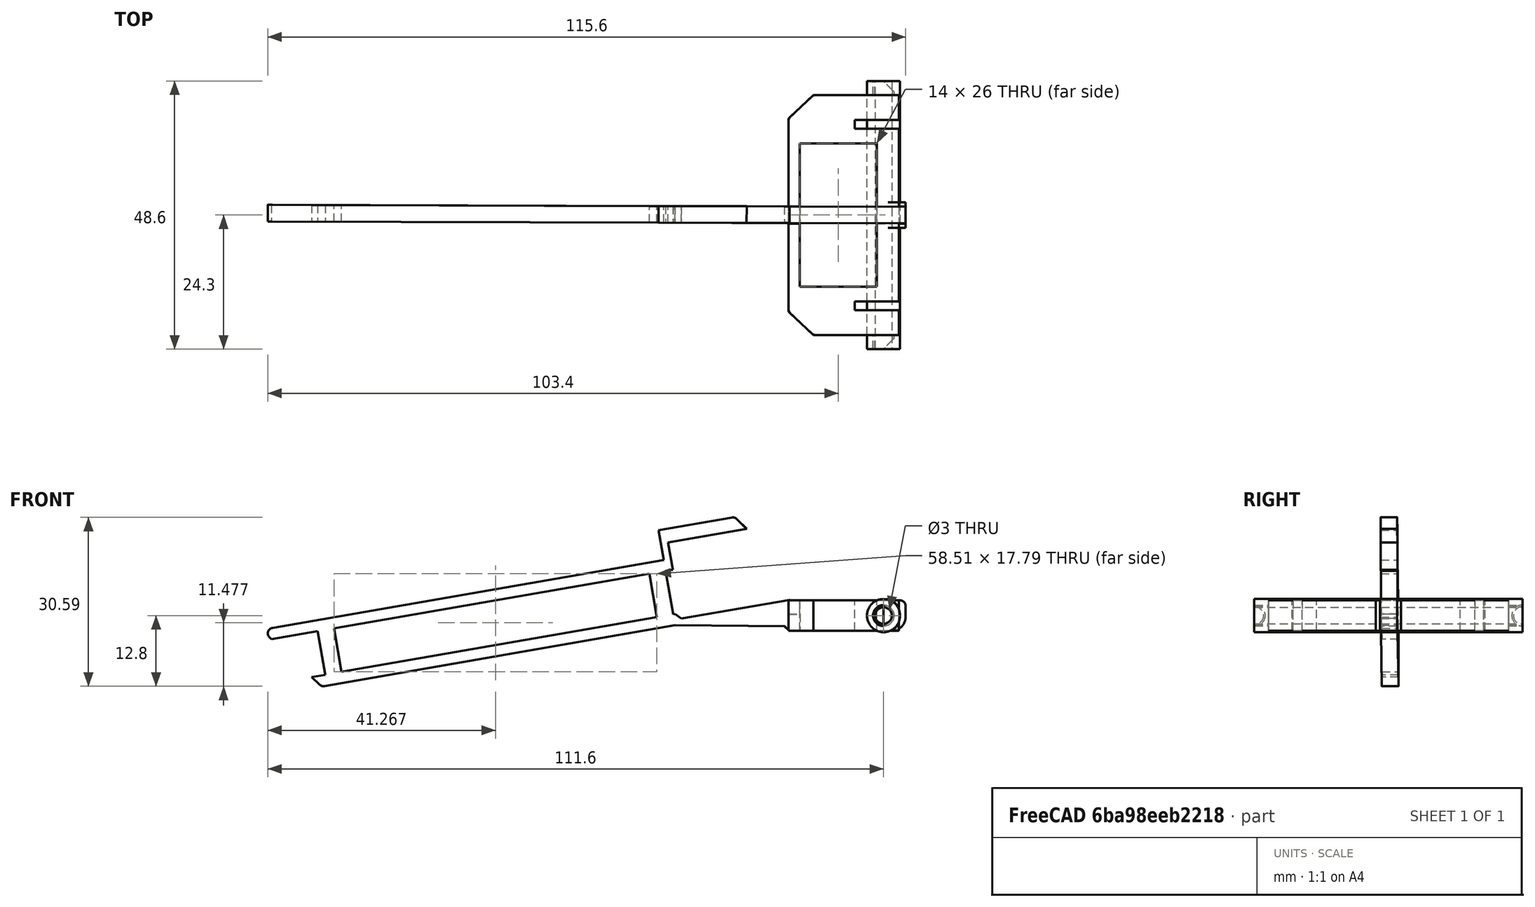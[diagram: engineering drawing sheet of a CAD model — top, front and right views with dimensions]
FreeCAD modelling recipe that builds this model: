
FCSTD DOCUMENT  (FreeCAD 0.20R29603 (Git))
Label: pieza_aspiradora_2
License: All rights reserved
LicenseURL: http://en.wikipedia.org/wiki/All_rights_reserved
objects: Part::Feature×11, Part::Cut×11, Part::Box×9, Part::Fillet×4, Part::Cylinder×3, Part::MultiFuse×3, Mesh::Feature×2, Sketcher::SketchObject×1, PartDesign::Pad×1, PartDesign::Body×1
note: 45 computed .brp shape members not serialized (recipe doc carries the construction recipe); baked Part::Feature solids carry a one-line shape summary decoded from their .brp

FEATURE [Sketcher::SketchObject] Sketch
  FullyConstrained = true
  MapMode = 5
  Support = -> [XY_Plane]
  sketch-geometry (14):
    g0: LineSegment StartX=-12 StartY=-17.5 StartZ=0 EndX=-12 EndY=17.5 EndZ=0
    g1: LineSegment StartX=-12 StartY=17.5 StartZ=0 EndX=-7.5 EndY=21.75 EndZ=0
    g2: LineSegment StartX=-7.5 StartY=21.75 StartZ=0 EndX=8 EndY=21.75 EndZ=0
    g3: LineSegment StartX=8 StartY=21.75 StartZ=0 EndX=8 EndY=17.25 EndZ=0
    g4: LineSegment StartX=8 StartY=17.25 StartZ=0 EndX=0 EndY=17.25 EndZ=0
    g5: LineSegment StartX=0 StartY=17.25 StartZ=0 EndX=0 EndY=15.65 EndZ=0
    g6: LineSegment StartX=0 StartY=15.65 StartZ=0 EndX=8 EndY=15.65 EndZ=0
    g7: LineSegment StartX=8 StartY=15.65 StartZ=0 EndX=8 EndY=-15.65 EndZ=0
    g8: LineSegment StartX=8 StartY=-15.65 StartZ=0 EndX=0 EndY=-15.65 EndZ=0
    g9: LineSegment StartX=0 StartY=-15.65 StartZ=0 EndX=0 EndY=-17.25 EndZ=0
    g10: LineSegment StartX=0 StartY=-17.25 StartZ=0 EndX=8 EndY=-17.25 EndZ=0
    g11: LineSegment StartX=8 StartY=-17.25 StartZ=0 EndX=8 EndY=-21.75 EndZ=0
    g12: LineSegment StartX=8 StartY=-21.75 StartZ=0 EndX=-7.5 EndY=-21.75 EndZ=0
    g13: LineSegment StartX=-7.5 StartY=-21.75 StartZ=0 EndX=-12 EndY=-17.5 EndZ=0
  constraints (41):
    c: Coincident(g0,g1)
    c: Coincident(g1,g2)
    c: Horizontal(g2)
    c: Coincident(g2,g3)
    c: Vertical(g3)
    c: Coincident(g3,g4)
    c: Horizontal(g4)
    c: Coincident(g4,g5)
    c: Vertical(g5)
    c: Coincident(g5,g6)
    c: Horizontal(g6)
    c: Coincident(g6,g7)
    c: Vertical(g7)
    c: Coincident(g7,g8)
    c: Horizontal(g8)
    c: Coincident(g8,g9)
    c: Vertical(g9)
    c: Coincident(g9,g10)
    c: Horizontal(g10)
    c: Coincident(g10,g11)
    c: Vertical(g11)
    c: Coincident(g11,g12)
    c: Horizontal(g12)
    c: Coincident(g12,g13)
    c: Coincident(g13,g0)
    c: Equal(g2,g12)
    c: Equal(g13,g1)
    c: Equal(g3,g11)
    c: Equal(g4,g6)
    c: Equal(g5,g9)
    c: Symmetric(g0,g0,g-1)
    c: DistanceX(g2,g11) = 0
    c: DistanceY(g0,g0) = 35
    c: DistanceY(g12,g1) = 43.5
    c: DistanceX(g0,g2) = 20
    c: Equal(g4,g10)
    c: DistanceY(g3,g2) = 4.5
    c: DistanceY(g6,g3) = 1.6
    c: DistanceX(g6,g6) = 8
    c: Vertical(g5,g-1)
    c: DistanceX(g12,g12) = 15.5
FEATURE [PartDesign::Pad] Pad
  Direction = (0,0,1)
  Length = 5.5
  Length2 = 10
  Profile = -> Sketch
  ReferenceAxis = -> Sketch [N_Axis]
  Refine = true
  Type = 0
FEATURE [PartDesign::Body] Body
  Group = -> [Sketch,Pad]
  Origin = -> Origin
  Tip = -> Pad
FEATURE [Part::Feature] Body001
  shape: bbox 20 x 43.5 x 5.5 mm, 16 faces (baked)
FEATURE [Part::Cylinder] Cylinder
  Angle = 360
  AttacherType = Attacher::AttachEngine3D
  FirstAngle = 0
  Height = 48.6
  Placement = pos=(5.2,24.3,2.75) rot=(1,0,0;1.5708rad)
  Radius = 1.9
  SecondAngle = 0
FEATURE [Part::Box] Box  label="Cube"
  AttacherType = Attacher::AttachEngine3D
  Height = 10
  Length = 10
  Placement = pos=(3,15.65,0) rot=(0,0,1;0rad)
  Width = 1.6
FEATURE [Part::Box] Box001  label="Cube001"
  AttacherType = Attacher::AttachEngine3D
  Height = 10
  Length = 10
  Placement = pos=(1,-17.25,0) rot=(1,0,0;0rad)
  Width = 1.6
FEATURE [Part::Box] Box002  label="Cube002"
  AttacherType = Attacher::AttachEngine3D
  Height = 10
  Length = 10
  Placement = pos=(7.6,-36,0) rot=(0,0,1;0.785398rad)
  Width = 10
FEATURE [Part::Box] Box003  label="Cube003"
  AttacherType = Attacher::AttachEngine3D
  Height = 10
  Length = 10
  Placement = pos=(7.6,21.86,0) rot=(0,0,1;0.785398rad)
  Width = 10
FEATURE [Part::Box] Box004  label="Cube004"
  AttacherType = Attacher::AttachEngine3D
  Height = 5.5
  Length = 9.2
  Placement = pos=(0,-2.3,0) rot=(0,0,1;0rad)
  Width = 4.6
FEATURE [Part::MultiFuse] Fusion
  Refine = true
  Shapes = -> [Body001,Box004]
FEATURE [Part::MultiFuse] Fusion001
  Refine = true
  Shapes = -> [Cylinder,Fusion]
FEATURE [Part::Cut] Cut
  Base = -> Fusion001
  Refine = true
  Tool = -> Box
FEATURE [Part::Cut] Cut001
  Base = -> Cut
  Refine = true
  Tool = -> Box001
FEATURE [Part::Cut] Cut002
  Base = -> Cut001
  Refine = true
  Tool = -> Box002
FEATURE [Part::Cut] Cut003
  Base = -> Cut002
  Refine = true
  Tool = -> Box003
FEATURE [Part::Fillet] Fillet
  Base = -> Cut003
  Edges = 8 edges r=2: [Edge15,Edge19,Edge23,Edge27,Edge33,Edge37,Edge41,Edge45]
FEATURE [Part::Fillet] Fillet003002
  Base = -> Fillet
  Edges = 1 edges r=2.5: [Edge15]
FEATURE [Part::Fillet] Fillet003003
  Base = -> Fillet003002
  Edges = 1 edges r=1: [Edge77]
FEATURE [Part::Fillet] Fillet003004
  Base = -> Fillet003003
  Edges = 4 edges r=1: [Edge75,Edge80,Edge81,Edge85]
FEATURE [Part::Feature] Fillet003004001  label="pieza2_solida2"
  shape: bbox 21.2 x 48.6 x 5.5 mm, 40 faces (baked)
FEATURE [Part::Feature] Fillet003004002  label="for_test"
  shape: bbox 21.2 x 48.6 x 5.5 mm, 40 faces (baked)
FEATURE [Part::Box] Box005  label="Cube005"
  AttacherType = Attacher::AttachEngine3D
  Height = 10
  Length = 14
  Placement = pos=(-10,-13,-2) rot=(0,0,1;0rad)
  Width = 26
FEATURE [Part::Cut] Cut004  label="test"
  Base = -> Fillet003004002
  Refine = true
  Tool = -> Box005
FEATURE [Part::Cylinder] Cylinder001
  Angle = 360
  AttacherType = Attacher::AttachEngine3D
  FirstAngle = 0
  Height = 48.6
  Placement = pos=(5.2,24.3,2.75) rot=(1,0,0;1.5708rad)
  Radius = 3
  SecondAngle = 0
FEATURE [Part::Cylinder] Cylinder002
  Angle = 360
  AttacherType = Attacher::AttachEngine3D
  FirstAngle = 0
  Height = 48.6
  Placement = pos=(5.2,24.3,2.75) rot=(1,0,0;1.5708rad)
  Radius = 1.5
  SecondAngle = 0
FEATURE [Part::Cut] Cut005
  Base = -> Cylinder001
  Tool = -> Cylinder002
FEATURE [Part::Feature] Cut005001  label="cilindro160"
  Placement = pos=(0,46.05,0) rot=(0,0,1;0rad)
  shape: bbox 6 x 48.6 x 6 mm, 4 faces (baked)
FEATURE [Part::Feature] Cut005002  label="cilindro161"
  Placement = pos=(0,-46.05,0) rot=(0,0,1;0rad)
  shape: bbox 6 x 48.6 x 6 mm, 4 faces (baked)
FEATURE [Part::Feature] Cut005003  label="cilindro162"
  shape: bbox 6 x 48.6 x 6 mm, 4 faces (baked)
FEATURE [Part::Feature] Cut005004  label="cilindro163"
  shape: bbox 6 x 48.6 x 6 mm, 4 faces (baked)
FEATURE [Part::Cut] Cut005005
  Base = -> Cut004
  Tool = -> Cut005001
FEATURE [Part::Cut] Cut005006  label="test_16"
  Base = -> Cut005005
  Tool = -> Cut005002
FEATURE [Part::Feature] Cut013014001  label="for_test001"
  Placement = pos=(-34.67,-15.37,12.8) rot=(-0.059649,0.705848,0.705848;3.0182rad)
  shape: bbox 115.6 x 3.353 x 30.59 mm, 36 faces (baked)
FEATURE [Part::Box] Box006  label="Cube006"
  AttacherType = Attacher::AttachEngine3D
  Height = 10
  Length = 45
  Placement = pos=(-8,-1.5,0) rot=(0,0,1;0rad)
  Width = 3.1
FEATURE [Part::Box] Box007  label="Cube007"
  AttacherType = Attacher::AttachEngine3D
  Height = 10
  Length = 45
  Placement = pos=(-50,-1.5,3) rot=(0,0,1;0rad)
  Width = 3.1
FEATURE [Part::Feature] Cut005006001  label="test_016_simple"
  shape: bbox 21.2 x 48.6 x 5.5 mm, 52 faces (baked)
FEATURE [Part::MultiFuse] Fusion002
  Placement = pos=(0,-0.05,0) rot=(0,0,1;0rad)
  Shapes = -> [Box007,Box006]
FEATURE [Part::Cut] Cut013014002  label="test_pieza_16_encastre"
  Base = -> Cut005006001
  Tool = -> Fusion002
FEATURE [Part::Feature] Cut013014002001
  shape: bbox 21.2 x 48.6 x 5.5 mm, 62 faces (baked)
FEATURE [Part::Cut] Cut013014002002
  Base = -> Cut013014001
  Tool = -> Cut013014002001
FEATURE [Part::Box] Box008  label="Cube008"
  AttacherType = Attacher::AttachEngine3D
  Height = 10
  Length = 2.1
  Placement = pos=(-12.05,-5,-6.95) rot=(0,0,1;0rad)
  Width = 10
FEATURE [Part::Cut] Cut013014002003  label="test_pieza_1_encastre"
  Base = -> Cut013014002002
  Tool = -> Box008
FEATURE [Mesh::Feature] Mesh  label="test_pieza_16_encastre (Meshed)"
FEATURE [Mesh::Feature] Mesh001  label="test_pieza_1_encastre (Meshed)"
FEATURE [Part::Feature] Cut005006002  label="cortador_15"
  shape: bbox 6 x 48.6 x 6 mm, 4 faces (baked)
